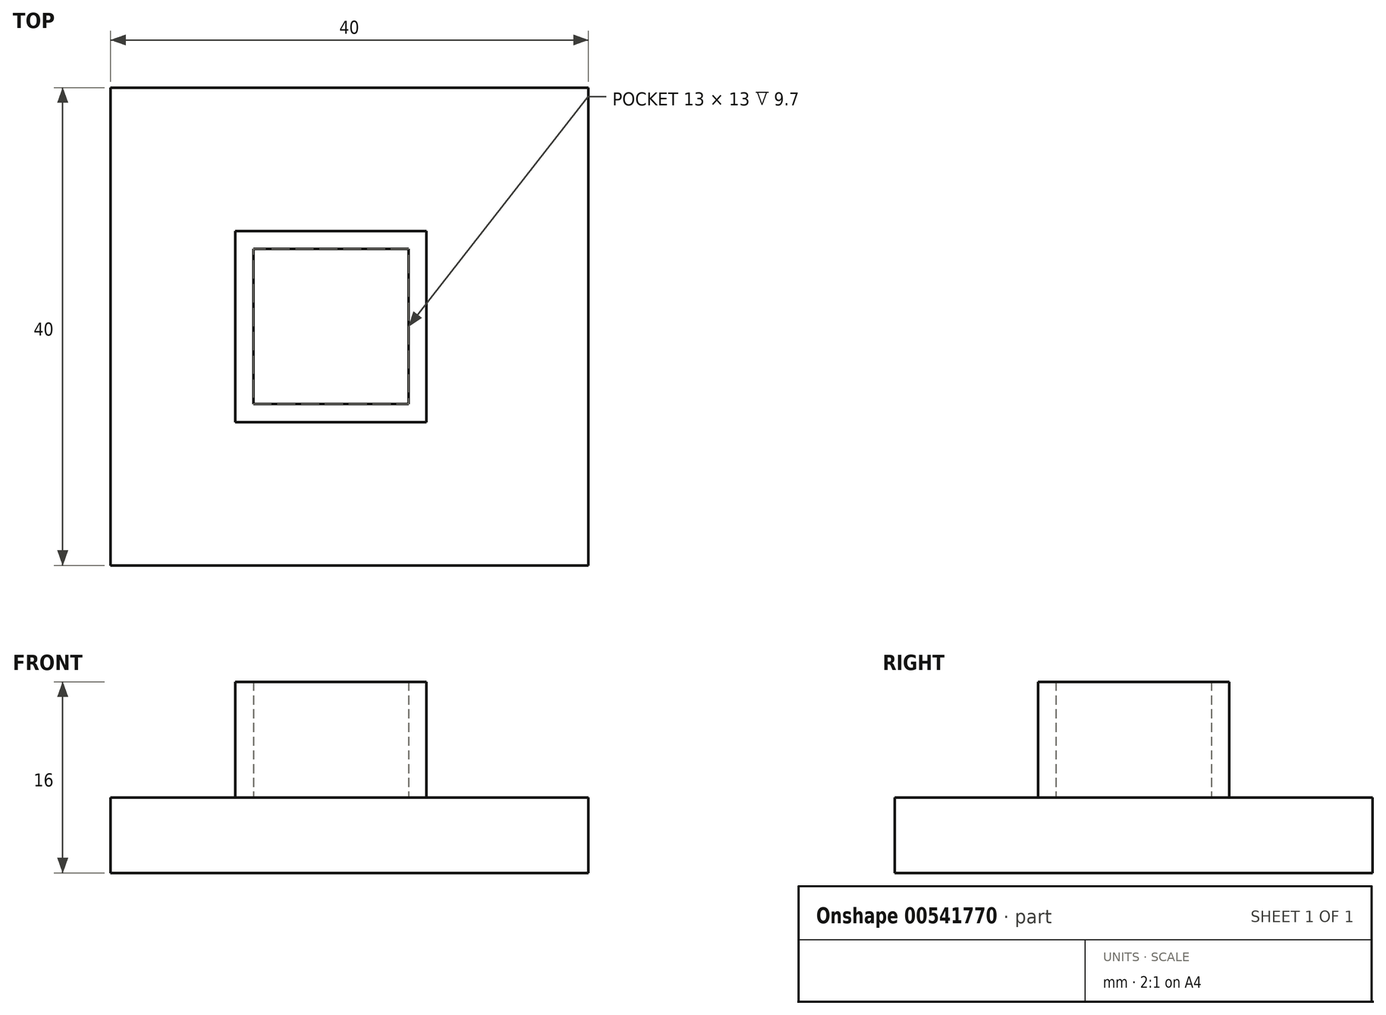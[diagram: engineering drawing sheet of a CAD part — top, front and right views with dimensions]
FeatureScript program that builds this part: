
annotation { "Feature Type Name" : "Feature", "Feature Type Description" : "" }
export const myFeature = defineFeature(function(context is Context, id is Id, definition is map)
    precondition{}
    {
        {
            var Q0;
            Q0=qCreatedBy(makeId("Top.planeOp"),FACE);
            var sketch = newSketch(context, id + "F0", { "sketchPlane" : qUnion([Q0])});
            skLineSegment(sketch, "E0.bottom", {"start": v(-8, 8) * mm, "end": v(8, 8) * mm});
            skLineSegment(sketch, "E0.top", {"start": v(-8, -8) * mm, "end": v(8, -8) * mm});
            skLineSegment(sketch, "E0.left", {"start": v(-8, 8) * mm, "end": v(-8, -8) * mm});
            skLineSegment(sketch, "E0.right", {"start": v(8, 8) * mm, "end": v(8, -8) * mm});
            skPoint(sketch, "E0.middle", {"position": v(0, 0) * mm});
            skLineSegment(sketch, "E1.bottom", {"start": v(-6.5, 6.5) * mm, "end": v(6.5, 6.5) * mm});
            skLineSegment(sketch, "E1.top", {"start": v(-6.5, -6.5) * mm, "end": v(6.5, -6.5) * mm});
            skLineSegment(sketch, "E1.left", {"start": v(-6.5, 6.5) * mm, "end": v(-6.5, -6.5) * mm});
            skLineSegment(sketch, "E1.right", {"start": v(6.5, 6.5) * mm, "end": v(6.5, -6.5) * mm});
            skSolve(sketch);
        }
        {
            var Q0;
            Q0=makeQuery(id+"F0.imprint","IMPRINT",FACE,{"disambiguationData":[TD([[makeQuery(id+"F0.imprint","IMPRINT",EDGE,{"derivedFrom":sQuery(id+"F0.wireOp",EDGE,"E0.bottom")}),-1.0]])]});
            extrude(context, id + "F1", {"entities" : qUnion([Q0]), "depth" : 16 * mm, "offsetDistance" : 25 * mm});
        }
        {
            var Q0;
            Q0=qCreatedBy(makeId("Top.planeOp"),FACE);
            var sketch = newSketch(context, id + "F2", { "sketchPlane" : qUnion([Q0])});
            skLineSegment(sketch, "E2.bottom", {"start": v(-18.45, -20) * mm, "end": v(21.55, -20) * mm});
            skLineSegment(sketch, "E2.left", {"start": v(-18.45, -20) * mm, "end": v(-18.45, 20) * mm});
            skLineSegment(sketch, "E2.right", {"start": v(21.55, -20) * mm, "end": v(21.55, 20) * mm});
            skPoint(sketch, "E3", {"position": v(0, 0) * mm});
            skPoint(sketch, "E4", {"position": v(0, 20) * mm});
            skLineSegment(sketch, "E5", {"start": v(0, 0) * mm, "end": v(0, 20) * mm});
            skLineSegment(sketch, "E6", {"start": v(-18.45, 20) * mm, "end": v(21.55, 20) * mm});
            skSolve(sketch);
        }
        {
            var Q0;
            Q0=makeQuery(id+"F2.imprint","IMPRINT",FACE,{"disambiguationData":[TD([[makeQuery(id+"F2.imprint","IMPRINT",EDGE,{"derivedFrom":sQuery(id+"F2.wireOp",EDGE,"E2.bottom")}),1.0]])]});
            extrude(context, id + "F3", {"entities" : qUnion([Q0]), "operationType" : NewBodyOperationType.ADD, "depth" : 6.3 * mm, "offsetDistance" : 25 * mm});
        }
    });
